# Revit family: Heater-QMark-Thermazone_Thin_Series
name_source: partatom
category: Mechanical Equipment
units: mm (PartAtom-declared; Revit-internal decimal feet)

## family parameters
Classification = None
Cut with Voids When Loaded = No
Host = Face
OmniClass Number = 23.75.70.17.17
OmniClass Title = Radiation Panels
Part Type = Normal
Room Calculation Point = No
Round Connector Dimension = Use Diameter
Shared = No

## types (14) — shared parameters
Assembly Code = D3060300
Default Elevation = 0' - 0"
Depth = 0' - 8"
Description = Infrared Heaters for Industrial/Commercial/Residential
Frequency = 60 Hz
Height = 0' - 9"
Infrared Material = Paint - QMark - Powder Coated Black
Instruction Sheet Link = https://www.marleymep.com
Keynote = 15500
Manufacturer = Marley® Engineered Products
Number of Poles = 1
Phase = 1
Power Factor = 1
Product Documentation Link = https://www.marleymep.com
Product Name = Thermazone Thin Series - Commercial/Residential Infrared Heater
Product Page URL = https://www.marleymep.com
URL = https://www.marleymep.com
Version = 2020 - v1.0a

## per-type parameters (varying)
| type | Amps | Length | Total Heating Capacity | Voltage | Watts |
| QR-STT-U18-1091B | 9 A | 2' - 0" | 3720.0 Btu/h | 120 V | 1091 W |
| QR-STT-U18-1330B | 12 A | 2' - 0" | 4538.0 Btu/h | 120 V | 1330 W |
| QR-STT-U18-1767B | 15 A | 2' - 0" | 6029.0 Btu/h | 120 V | 1767 W |
| QR-STT-U18-2161B | 18 A | 2' - 0" | 7373.0 Btu/h | 120 V | 2161 W |
| QR-STT-U36-2180V | 7 A | 3' - 6" | 7438.0 Btu/h | 208 V | 2180 W |
| QR-STT-U36-1635V | 9 A | 3' - 6" | 5578.0 Btu/h | 240 V | 1635 W |
| QR-STT-U36-2660V | 9 A | 3' - 6" | 9076.0 Btu/h | 208 V | 2660 W |
| QR-STT-U36-2071V | 12 A | 3' - 6" | 7066.0 Btu/h | 240 V | 2071 W |
| QR-STT-U36-3104V | 10 A | 3' - 6" | 10591.0 Btu/h | 208 V | 3104 W |
| QR-STT-U36-2328V | 13 A | 3' - 6" | 7943.0 Btu/h | 240 V | 2328 W |
| QR-STT-U36-3534V | 11 A | 3' - 6" | 12058.0 Btu/h | 208 V | 3534 W |
| QR-STT-U36-2661V | 15 A | 3' - 6" | 9079.0 Btu/h | 240 V | 2661 W |
| QR-STT-U36-4322V | 16 A | 3' - 6" | 14747.0 Btu/h | 208 V | 4322 W |
| QR-STT-U36-3242V | 18 A | 3' - 6" | 11062.0 Btu/h | 240 V | 3242 W |

note: column(s) folded — value = type name in every type: Model

## geometry (parser evidence)
native form markers: Sweep x2
no freeform markers — native parametric forms only
